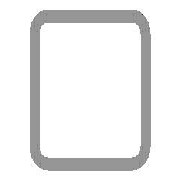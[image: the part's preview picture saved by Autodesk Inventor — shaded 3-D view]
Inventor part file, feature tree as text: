
AUTODESK INVENTOR PART (.ipt)
format: ipt  version: 2025 (Build 290162010, 162A)  size: 129,536 bytes
history: native  units: mm (DEFAULTED — no unit token found)
features: other x3, sketch x1, plane x1
ambient origin geometry x8: Origin, YZ Plane, XZ Plane, XY Plane, X Axis, Y Axis, Z Axis, Center Point
bodies: Solid1 (feature_tree), Body (feature_tree)
feature tree (5):
  other  "Driven Length"
  other  "Start plane"
  other  "End plane"
  sketch  "Sketch3"  dims[d3=1000.0mm d4=0.0mm d7=4.0mm d9=40.0mm d11=40.0mm d12=2.0mm d13=-0.0mm d14=1000.0mm d15=20.0mm d16=20.0mm d17=90.0deg d18=1000.0mm]
  plane  "Work Plane3"
